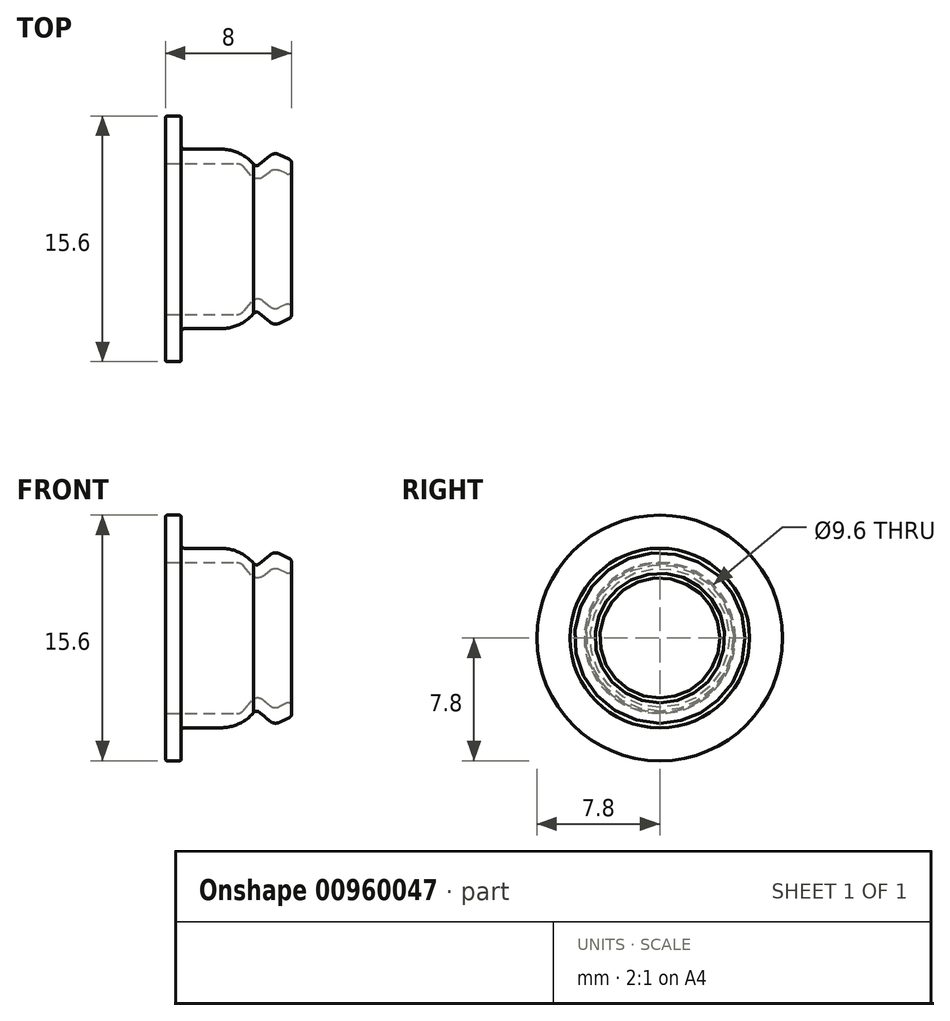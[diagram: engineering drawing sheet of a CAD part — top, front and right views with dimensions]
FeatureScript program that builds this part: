
annotation { "Feature Type Name" : "Feature", "Feature Type Description" : "" }
export const myFeature = defineFeature(function(context is Context, id is Id, definition is map)
    precondition{}
    {
        {
            var Q0;
            Q0=qCreatedBy(makeId("Front.planeOp"),FACE);
            var sketch = newSketch(context, id + "F0", { "sketchPlane" : qUnion([Q0])});
            skLineSegment(sketch, "E0", {"start": v(0, 0) * mm, "end": v(-43.58, 0) * mm, "construction": true});
            skLineSegment(sketch, "E1", {"start": v(-0.14, 5.07) * mm, "end": v(-0.77, 5.36) * mm});
            skLineSegment(sketch, "E2", {"start": v(-1.36, 5.28) * mm, "end": v(-2.05, 4.7) * mm});
            skLineSegment(sketch, "E3", {"start": v(-2.38, 4.7) * mm, "end": v(-2.4, 4.74) * mm});
            skLineSegment(sketch, "E4", {"start": v(-4.49, 5.7) * mm, "end": v(-6.8, 5.7) * mm});
            skLineSegment(sketch, "E5", {"start": v(-7, 5.9) * mm, "end": v(-7, 7.7) * mm});
            skLineSegment(sketch, "E6", {"start": v(-7.1, 7.8) * mm, "end": v(-7.9, 7.8) * mm});
            skLineSegment(sketch, "E7", {"start": v(-8, 7.7) * mm, "end": v(-8, 4.9) * mm});
            skLineSegment(sketch, "E8", {"start": v(-7.9, 4.8) * mm, "end": v(-3.47, 4.8) * mm});
            skLineSegment(sketch, "E9", {"start": v(-3.05, 4.6) * mm, "end": v(-2.56, 4.02) * mm});
            skLineSegment(sketch, "E10", {"start": v(-1.79, 3.94) * mm, "end": v(-1.37, 4.3) * mm});
            skLineSegment(sketch, "E11", {"start": v(-0.79, 4.37) * mm, "end": v(-0.3, 4.14) * mm});
            skLineSegment(sketch, "E12", {"start": v(0, 4.33) * mm, "end": v(0, 4.84) * mm});
            skPoint(sketch, "E13.visualSharp", {"position": v(-1.09, 5.5) * mm});
            skArc(sketch, "E13.filletArc", {"start": v(-0.77, 5.36) * mm, "mid": v(-1.07, 5.4) * mm, "end": v(-1.36, 5.28) * mm});
            skPoint(sketch, "E14.visualSharp", {"position": v(-1.1, 4.51) * mm});
            skArc(sketch, "E14.filletArc", {"start": v(-0.79, 4.37) * mm, "mid": v(-1.1, 4.41) * mm, "end": v(-1.37, 4.3) * mm});
            skPoint(sketch, "E15.visualSharp", {"position": v(-3.22, 4.8) * mm});
            skArc(sketch, "E15.filletArc", {"start": v(-3.05, 4.6) * mm, "mid": v(-3.24, 4.75) * mm, "end": v(-3.47, 4.8) * mm});
            skPoint(sketch, "E16.visualSharp", {"position": v(-2.21, 3.6) * mm});
            skArc(sketch, "E16.filletArc", {"start": v(-2.56, 4.02) * mm, "mid": v(-2.2, 3.82) * mm, "end": v(-1.79, 3.94) * mm});
            skPoint(sketch, "E17.visualSharp", {"position": v(-2.24, 4.55) * mm});
            skArc(sketch, "E17.filletArc", {"start": v(-2.4, 4.74) * mm, "mid": v(-2.23, 4.65) * mm, "end": v(-2.05, 4.7) * mm});
            skPoint(sketch, "E18.visualSharp", {"position": v(-3.2, 5.7) * mm});
            skArc(sketch, "E18.filletArc", {"start": v(-2.38, 4.7) * mm, "mid": v(-3.32, 5.44) * mm, "end": v(-4.49, 5.7) * mm});
            skPoint(sketch, "E19.visualSharp", {"position": v(0, 5) * mm});
            skArc(sketch, "E19.filletArc", {"start": v(0, 4.84) * mm, "mid": v(-0.04, 4.98) * mm, "end": v(-0.14, 5.07) * mm});
            skPoint(sketch, "E20.visualSharp", {"position": v(0, 4) * mm});
            skArc(sketch, "E20.filletArc", {"start": v(-0.3, 4.14) * mm, "mid": v(-0.1, 4.15) * mm, "end": v(0, 4.33) * mm});
            skPoint(sketch, "E21.visualSharp", {"position": v(-8, 4.8) * mm});
            skArc(sketch, "E21.filletArc", {"start": v(-8, 4.9) * mm, "mid": v(-7.97, 4.83) * mm, "end": v(-7.9, 4.8) * mm});
            skPoint(sketch, "E22.visualSharp", {"position": v(-7, 5.7) * mm});
            skArc(sketch, "E22.filletArc", {"start": v(-7, 5.9) * mm, "mid": v(-6.94, 5.76) * mm, "end": v(-6.8, 5.7) * mm});
            skPoint(sketch, "E23.visualSharp", {"position": v(-8, 7.8) * mm});
            skArc(sketch, "E23.filletArc", {"start": v(-7.9, 7.8) * mm, "mid": v(-7.97, 7.77) * mm, "end": v(-8, 7.7) * mm});
            skPoint(sketch, "E24.visualSharp", {"position": v(-7, 7.8) * mm});
            skArc(sketch, "E24.filletArc", {"start": v(-7, 7.7) * mm, "mid": v(-7.03, 7.77) * mm, "end": v(-7.1, 7.8) * mm});
            skSolve(sketch);
        }
        {
            var Q0;
            Q0 = qSketchRegion(id + "F0", true);
            var Q1;
            Q1=sQuery(id+"F0.wireOp",EDGE,"E0");
            revolve(context, id + "F1", {"surfaceOperationType" : NewSurfaceOperationType.NEW, "entities" : qUnion([Q0]), "axis" : qUnion([Q1]), "revolveType" : RevolveType.FULL});
        }
    });
